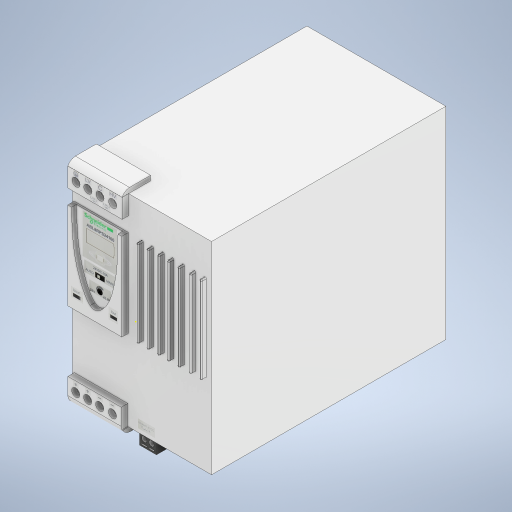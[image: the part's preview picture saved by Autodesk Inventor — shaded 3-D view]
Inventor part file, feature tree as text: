
AUTODESK INVENTOR PART (.ipt)
format: ipt  version: 2023 (Build 270158000, 158)  size: 1,285,632 bytes
history: native  units: in
note: dims shown in document units (in); Inventor stores cm internally (conversion verified against a paired STEP export)
features: other x33, sketch x15, extrude x12, fillet x6
ambient origin geometry x8: Origin, YZ Plane, XZ Plane, XY Plane, X Axis, Y Axis, Z Axis, Center Point
bodies: Solid1 (feature_tree)
feature tree (66):
  extrude  "Extrusion1"  Depth=3.3858in
  sketch  "Sketch2"  dims[d2=5.7087in d3=0.0in d4=0.1575in d5=0.0in]
  extrude  "Extrusion2"  Depth=0.1575in TaperAngle=0.0deg
  extrude  "Extrusion3"  Depth=0.1181in TaperAngle=0.0deg
  extrude  "Extrusion4"  Depth=0.0276in
  fillet  "Fillet1"  Radius=0.0276in
  fillet  "Fillet2"  Radius=0.0276in
  fillet  "Fillet3"  Radius=0.1181in
  fillet  "Fillet4"  Radius=0.1969in
  extrude  "Extrusion5"  Depth=0.1969in
  fillet  "Fillet5"  Radius=0.1181in
  extrude  "Extrusion6"  Depth=0.2in
  fillet  "Fillet6"  Radius=0.2in
  sketch  "Sketch5"  dims[d17=0.1181in d18=0.0in d19=0.1969in d42=0.1181in d43=0.0in]
  extrude  "Extrusion7"  Depth=0.2in
  sketch  "Sketch7"  dims[d120=0.2in d121=0.2in d122=0.2in d123=0.2in d124=0.2in]
  other  "Decal1"
  other  "Decal2"
  other  "Decal3"
  sketch  "Sketch8"  dims[d125=0.1181in d126=0.0in d127=0.1181in d128=0.0in]
  other  "Decal4"
  other  "Decal5"
  sketch  "Sketch9"  dims[d358=0.2756in d359=0.0in d360=0.2756in d361=0.0in]
  sketch  "Sketch10"  dims[d362=0.1575in d363=0.0in]
  extrude  "Extrusion8"  Depth=0.1181in TaperAngle=0.0deg
  extrude  "Extrusion9"  Depth=0.2756in TaperAngle=0.0deg
  sketch  "Sketch11"
  other  "Decal6"
  other  "Decal7"
  other  "Decal8"
  other  "Decal9"
  sketch  "Sketch12"
  other  "Decal10"
  other  "Decal11"
  other  "Decal12"
  other  "Decal13"
  other  "Decal14"
  other  "Decal15"
  extrude  "Extrusion10"  [1 undecoded]
  sketch  "Sketch14"
  extrude  "Extrusion11"  [1 undecoded]
  extrude  "Extrusion12"  [1 undecoded]
  other  "Decal16"
  sketch  "Sketch1"  dims[d0=4.9213in d1=3.3858in]
  sketch  "Sketch3"  dims[d6=0.1575in d7=0.0in d8=0.1181in d9=0.0in]
  sketch  "Sketch4"  dims[d10=0.0276in d11=0.0276in d12=0.0276in d13=0.0276in d14=0.1181in d15=0.0in d16=0.1969in]
  sketch  "Sketch6"  dims[d117=0.2in d118=0.2in d119=0.2in]
  other  "Image1"
  other  "Image2"
  other  "Image3"
  other  "Image4"
  other  "Image5"
  other  "Image6"
  other  "Image7"
  other  "Image8"
  other  "Image9"
  other  "Image10"
  other  "Image11"
  other  "Image12"
  other  "Image13"
  other  "Image14"
  other  "Image15"
  other  "Image16"
  sketch  "Sketch13"
  sketch  "Sketch15"
  other  "Image17"
note: 3 required parameter values undecoded (feature->parameter linkage not recoverable at this tier; creation-order binding heuristic only, values carry confidence <= 0.55)
